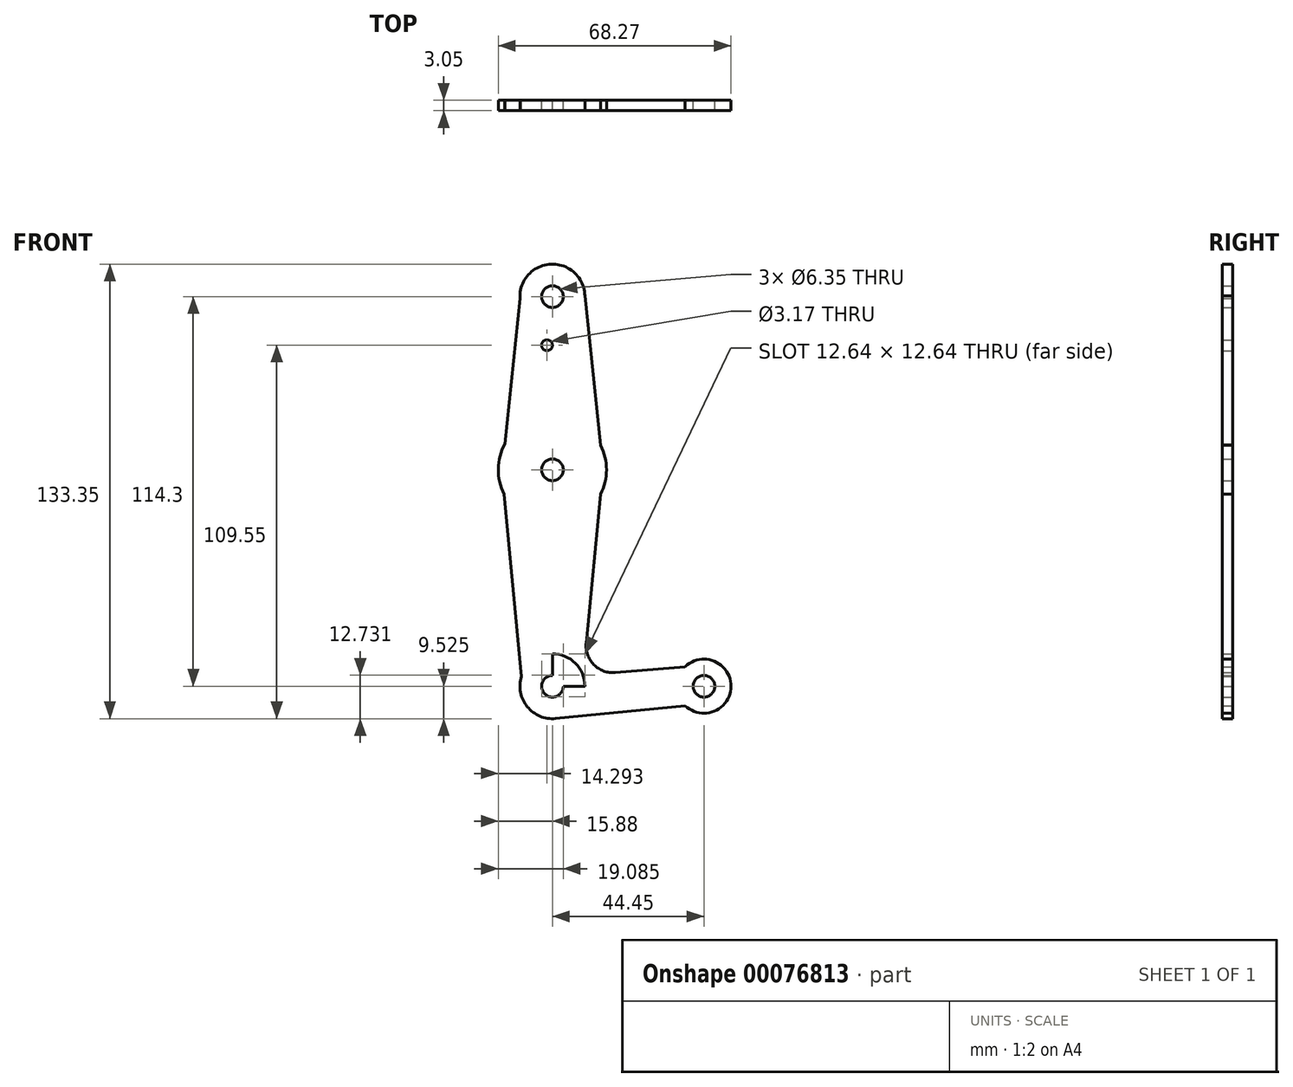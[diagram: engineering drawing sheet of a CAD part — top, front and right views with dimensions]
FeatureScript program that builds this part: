
annotation { "Feature Type Name" : "Feature", "Feature Type Description" : "" }
export const myFeature = defineFeature(function(context is Context, id is Id, definition is map)
    precondition{}
    {
        {
            var Q0;
            Q0=qCreatedBy(makeId("Front.planeOp"),FACE);
            var sketch = newSketch(context, id + "F0", { "sketchPlane" : qUnion([Q0])});
            skLineSegment(sketch, "E0", {"start": v(0, 70.59) * mm, "end": v(0, 0) * mm});
            skLineSegment(sketch, "E1", {"start": v(0, 0) * mm, "end": v(0, -43.71) * mm});
            skLineSegment(sketch, "E2", {"start": v(0, -43.71) * mm, "end": v(44.45, -43.71) * mm});
            skCircle(sketch, "E3", {"center": v(0, 70.59) * mm, "radius": 9.53 * mm});
            skCircle(sketch, "E4", {"center": v(0, 19.79) * mm, "radius": 15.88 * mm});
            skCircle(sketch, "E5", {"center": v(0, -43.71) * mm, "radius": 9.53 * mm});
            skCircle(sketch, "E6", {"center": v(44.45, -43.71) * mm, "radius": 7.94 * mm});
            skLineSegment(sketch, "E7", {"start": v(-9.5, 70.04) * mm, "end": v(-13.94, 27.38) * mm});
            skLineSegment(sketch, "E8", {"start": v(-14.17, 12.62) * mm, "end": v(-9.08, -40.85) * mm});
            skLineSegment(sketch, "E9", {"start": v(9.52, 70.76) * mm, "end": v(14.16, 26.96) * mm});
            skLineSegment(sketch, "E10", {"start": v(14.16, 12.61) * mm, "end": v(9.9, -31.02) * mm});
            skLineSegment(sketch, "E11", {"start": v(18.48, -39.72) * mm, "end": v(38.95, -38) * mm});
            skLineSegment(sketch, "E12", {"start": v(38.95, -49.44) * mm, "end": v(0, -53.29) * mm});
            skCircle(sketch, "E13", {"center": v(0, 70.59) * mm, "radius": 3.18 * mm});
            skCircle(sketch, "E14", {"center": v(-1.59, 56.31) * mm, "radius": 1.59 * mm});
            skCircle(sketch, "E15", {"center": v(0, 19.79) * mm, "radius": 3.18 * mm});
            skCircle(sketch, "E16", {"center": v(0, -43.71) * mm, "radius": 3.18 * mm});
            skCircle(sketch, "E17", {"center": v(44.45, -43.71) * mm, "radius": 3.18 * mm});
            skPoint(sketch, "E18.visualSharp", {"position": v(8.97, -40.52) * mm});
            skArc(sketch, "E18.filletArc", {"start": v(9.9, -31.02) * mm, "mid": v(12.15, -37.38) * mm, "end": v(18.48, -39.72) * mm});
            skSolve(sketch);
        }
        {
            var Q0;
            Q0 = qSketchRegion(id + "F0", true);
            extrude(context, id + "F1", {"entities" : qUnion([Q0]), "depth" : 3.05 * mm});
        }
    });
